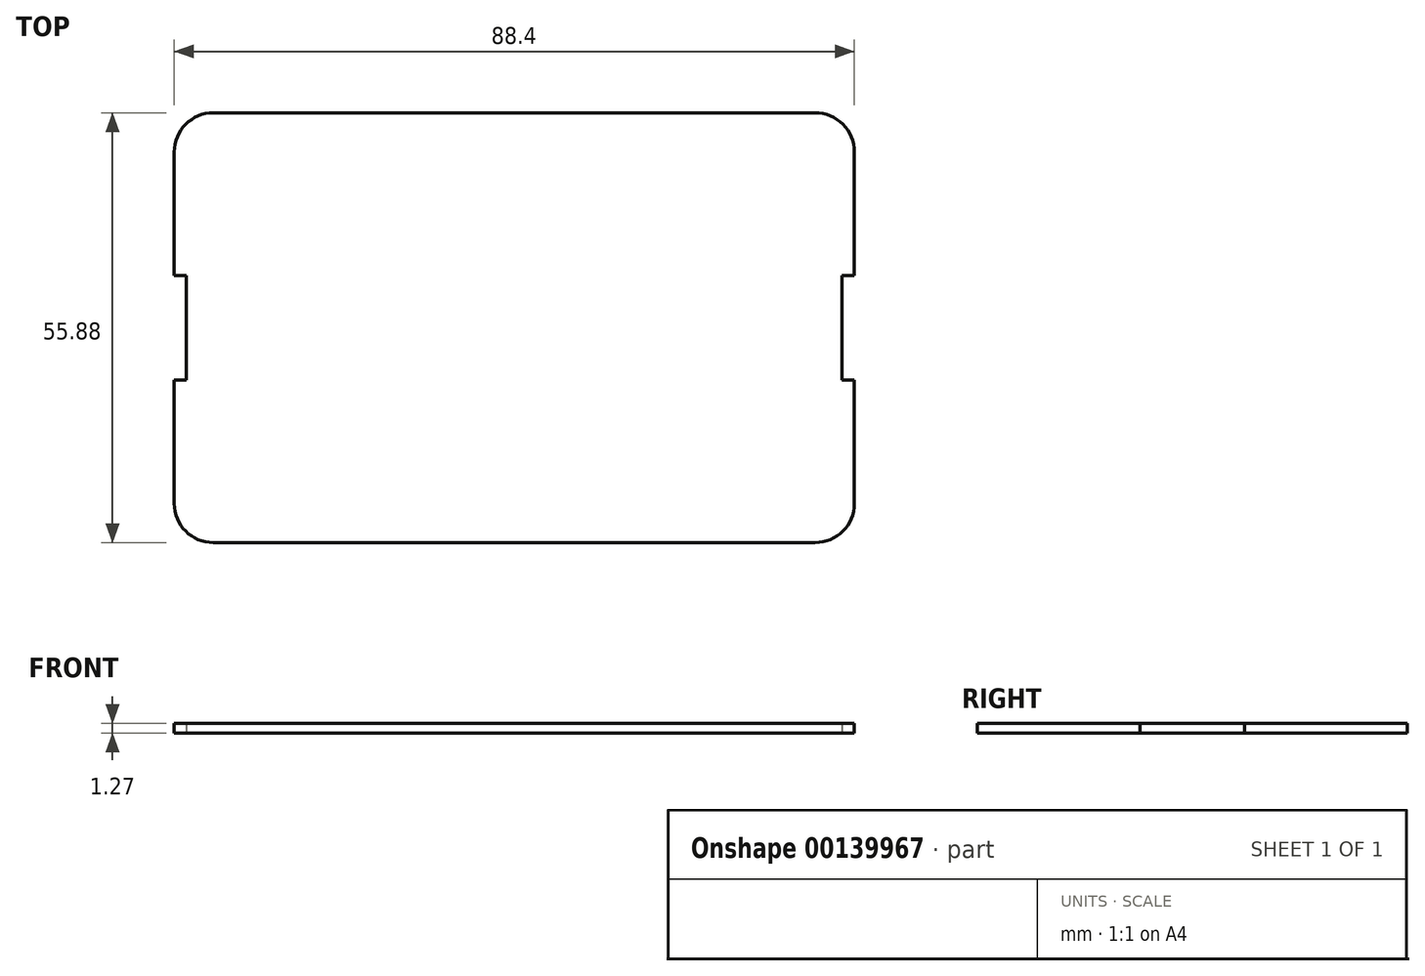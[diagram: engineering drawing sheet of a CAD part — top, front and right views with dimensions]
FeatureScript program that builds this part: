
annotation { "Feature Type Name" : "Feature", "Feature Type Description" : "" }
export const myFeature = defineFeature(function(context is Context, id is Id, definition is map)
    precondition{}
    {
        {
            var Q0;
            Q0=qCreatedBy(makeId("Top.planeOp"),FACE);
            var sketch = newSketch(context, id + "F0", { "sketchPlane" : qUnion([Q0])});
            skLineSegment(sketch, "E0.bottom", {"start": v(39.12, 27.94) * mm, "end": v(-39.12, 27.94) * mm});
            skLineSegment(sketch, "E0.top", {"start": v(39.12, -27.94) * mm, "end": v(-39.12, -27.94) * mm});
            skLineSegment(sketch, "E0.left", {"start": v(44.2, 22.86) * mm, "end": v(44.2, 6.8) * mm});
            skLineSegment(sketch, "E0.right", {"start": v(-44.2, 22.86) * mm, "end": v(-44.2, 6.8) * mm});
            skPoint(sketch, "E0.middle", {"position": v(0, 0) * mm});
            skLineSegment(sketch, "E1.left", {"start": v(43.5, 6.8) * mm, "end": v(43.5, -6.8) * mm});
            skLineSegment(sketch, "E1.right", {"start": v(-43.5, 6.8) * mm, "end": v(-43.5, -6.8) * mm});
            skPoint(sketch, "E2.visualSharp", {"position": v(-44.2, 27.94) * mm});
            skArc(sketch, "E2.filletArc", {"start": v(-39.12, 27.94) * mm, "mid": v(-42.7, 26.45) * mm, "end": v(-44.2, 22.86) * mm});
            skPoint(sketch, "E3.visualSharp", {"position": v(44.2, 27.94) * mm});
            skArc(sketch, "E3.filletArc", {"start": v(44.2, 22.86) * mm, "mid": v(42.7, 26.45) * mm, "end": v(39.12, 27.94) * mm});
            skPoint(sketch, "E4.visualSharp", {"position": v(44.2, -27.94) * mm});
            skArc(sketch, "E4.filletArc", {"start": v(39.12, -27.94) * mm, "mid": v(42.7, -26.45) * mm, "end": v(44.2, -22.86) * mm});
            skPoint(sketch, "E5.visualSharp", {"position": v(-44.2, -27.94) * mm});
            skArc(sketch, "E5.filletArc", {"start": v(-44.2, -22.86) * mm, "mid": v(-42.7, -26.45) * mm, "end": v(-39.12, -27.94) * mm});
            skLineSegment(sketch, "E6", {"start": v(-43.5, 6.8) * mm, "end": v(-44.2, 6.8) * mm});
            skLineSegment(sketch, "E7", {"start": v(-43.5, -6.8) * mm, "end": v(-44.2, -6.8) * mm});
            skLineSegment(sketch, "E8", {"start": v(43.5, 6.8) * mm, "end": v(44.2, 6.8) * mm});
            skLineSegment(sketch, "E9", {"start": v(43.5, -6.8) * mm, "end": v(44.2, -6.8) * mm});
            skLineSegment(sketch, "E10.trimOffspring", {"start": v(44.2, -6.8) * mm, "end": v(44.2, -22.86) * mm});
            skLineSegment(sketch, "E11.trimOffspring", {"start": v(-44.2, -6.8) * mm, "end": v(-44.2, -22.86) * mm});
            skLineSegment(sketch, "E12.bottom", {"start": v(-44.2, 6.8) * mm, "end": v(-42.8, 6.8) * mm});
            skLineSegment(sketch, "E12.top", {"start": v(-44.2, -6.8) * mm, "end": v(-42.8, -6.8) * mm});
            skLineSegment(sketch, "E12.left", {"start": v(-44.2, 6.8) * mm, "end": v(-44.2, -6.8) * mm});
            skLineSegment(sketch, "E12.right", {"start": v(-42.8, 6.8) * mm, "end": v(-42.8, -6.8) * mm});
            skLineSegment(sketch, "E13.bottom", {"start": v(44.2, 6.8) * mm, "end": v(42.8, 6.8) * mm});
            skLineSegment(sketch, "E13.top", {"start": v(44.2, -6.8) * mm, "end": v(42.8, -6.8) * mm});
            skLineSegment(sketch, "E13.left", {"start": v(44.2, 6.8) * mm, "end": v(44.2, -6.8) * mm});
            skLineSegment(sketch, "E13.right", {"start": v(42.8, 6.8) * mm, "end": v(42.8, -6.8) * mm});
            skLineSegment(sketch, "E14.bottom", {"start": v(-44.2, 6.8) * mm, "end": v(-42.6, 6.8) * mm});
            skLineSegment(sketch, "E14.top", {"start": v(-44.2, -6.8) * mm, "end": v(-42.6, -6.8) * mm});
            skLineSegment(sketch, "E14.right", {"start": v(-42.6, 6.8) * mm, "end": v(-42.6, -6.8) * mm});
            skLineSegment(sketch, "E15.bottom", {"start": v(44.2, 6.8) * mm, "end": v(42.6, 6.8) * mm});
            skLineSegment(sketch, "E15.top", {"start": v(44.2, -6.8) * mm, "end": v(42.6, -6.8) * mm});
            skLineSegment(sketch, "E15.right", {"start": v(42.6, 6.8) * mm, "end": v(42.6, -6.8) * mm});
            skSolve(sketch);
        }
        {
            var Q0;
            Q0=makeQuery(id+"F0.imprint","IMPRINT",FACE,{"disambiguationData":[TD([[makeQuery(id+"F0.imprint","IMPRINT",EDGE,{"derivedFrom":sQuery(id+"F0.wireOp",EDGE,"E0.bottom")}),1.0]])]});
            extrude(context, id + "F1", {"entities" : qUnion([Q0]), "depth" : 1.27 * mm});
        }
    });
